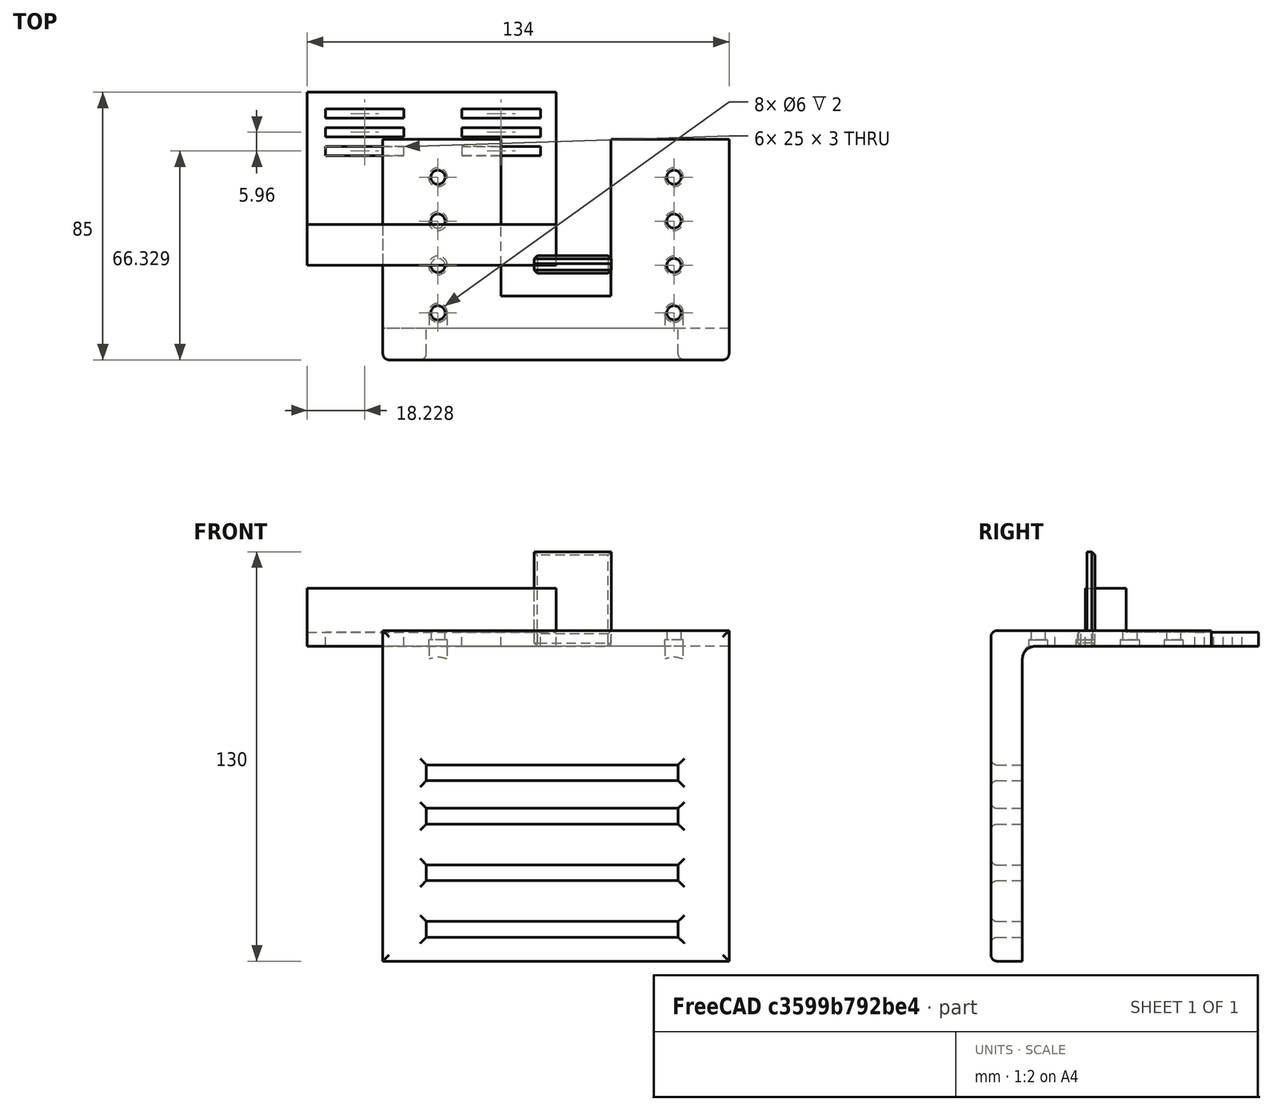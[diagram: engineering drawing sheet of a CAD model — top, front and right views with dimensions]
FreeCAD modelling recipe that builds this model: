
FCSTD DOCUMENT  (FreeCAD 1.2R20251230 (Git shallow))
Label: hook_1
License: Creative Commons Attribution 4.0
LicenseURL: https://creativecommons.org/licenses/by/4.0/
objects: TechDraw::DrawProjGroupItem×30, Sketcher::SketchObject×8, App::FeaturePython×8, PartDesign::Pad×5, App::Point×4, PartDesign::Pocket×3, PartDesign::Body×3, App::Link×3, TechDraw::DrawSVGTemplate×3, TechDraw::DrawProjGroup×3, TechDraw::DrawPage×3, PartDesign::Fillet×2, Assembly::JointGroup×1, PartDesign::Chamfer×1, Assembly::ViewGroup×1, Assembly::AssemblyObject×1
note: 52 computed .brp shape members not serialized (recipe doc carries the construction recipe); baked Part::Feature solids carry a one-line shape summary decoded from their .brp

FEATURE [App::Point] Origin001  label="原点"
  Role = Origin
FEATURE [Sketcher::SketchObject] Sketch
  ArcFitTolerance = 1e-06
  AttachmentSupport = -> [Origin]
  ExternalTypes = [0]
  FullyConstrained = false
  MakeInternals = false
  MapMode = 5
  sketch-geometry (16):
    g0: LineSegment StartX=-55 StartY=40 StartZ=0 EndX=-55 EndY=-30 EndZ=0
    g1: LineSegment StartX=-55 StartY=-30 StartZ=0 EndX=55 EndY=-30 EndZ=0
    g2: LineSegment StartX=55 StartY=-30 StartZ=0 EndX=55 EndY=40 EndZ=0
    g3: LineSegment StartX=55 StartY=40 StartZ=0 EndX=17.5 EndY=40 EndZ=0
    g4: Circle CenterX=-37.5 CenterY=0 CenterZ=0 NormalX=0 NormalY=0 NormalZ=1 AngleXU=0 Radius=2.25
    g5: Circle CenterX=37.5 CenterY=0 CenterZ=0 NormalX=0 NormalY=0 NormalZ=1 AngleXU=0 Radius=2.25
    g6: Circle CenterX=-37.5 CenterY=14.0912 CenterZ=0 NormalX=0 NormalY=0 NormalZ=1 AngleXU=0 Radius=2.25
    g7: Circle CenterX=37.5 CenterY=14.0912 CenterZ=0 NormalX=0 NormalY=0 NormalZ=1 AngleXU=0 Radius=2.25
    g8: Circle CenterX=-37.5 CenterY=-15.0582 CenterZ=0 NormalX=0 NormalY=0 NormalZ=1 AngleXU=0 Radius=2.25
    g9: Circle CenterX=37.5 CenterY=-15.0582 CenterZ=0 NormalX=0 NormalY=0 NormalZ=1 AngleXU=0 Radius=2.25
    g10: Circle CenterX=-37.5 CenterY=28.0083 CenterZ=0 NormalX=0 NormalY=0 NormalZ=1 AngleXU=0 Radius=2.25
    g11: Circle CenterX=37.5 CenterY=28.0083 CenterZ=0 NormalX=0 NormalY=0 NormalZ=1 AngleXU=0 Radius=2.25
    g12: LineSegment StartX=17.5 StartY=40 StartZ=0 EndX=17.5 EndY=-9.65989 EndZ=0
    g13: LineSegment StartX=17.5 StartY=-9.65989 StartZ=0 EndX=-17.5 EndY=-9.65989 EndZ=0
    g14: LineSegment StartX=-17.5 StartY=-9.65989 StartZ=0 EndX=-17.5 EndY=40 EndZ=0
    g15: LineSegment StartX=-17.5 StartY=40 StartZ=0 EndX=-55 EndY=40 EndZ=0
  constraints (27):
    c: Coincident(g0,g1)
    c: Coincident(g1,g2)
    c: Coincident(g2,g3)
    c: Coincident(g15,g0)
    c: Vertical(g2)
    c: Horizontal(g1)
    c: Symmetric(g2,g0,g-2)
    c: DistanceY(g0,g0) = 70
    c: DistanceX(g15,g3) = 110
    c: PointOnObject(g4,g-1)
    c: Symmetric(g4,g5,g-2)
    c: Distance(g1,g-1) = 30
    c: Diameter(g10) = 4.5
    c: Diameter(g11) = 4.5
    c: Diameter(g7) = 4.5
    c: Diameter(g6) = 4.5
    c: Diameter(g8) = 4.5
    c: Diameter(g9) = 4.5
    c: Diameter(g5) = 4.5
    c: Diameter(g4) = 4.5
    c: Coincident(g12,g13)
    c: Coincident(g13,g14)
    c: Symmetric(g12,g13,g-2)
    c: Vertical(g12)
    c: Vertical(g14)
    c: Coincident(g12,g3)
    c: Coincident(g14,g15)
FEATURE [PartDesign::Pad] Pad
  Direction = (0,0,1)
  Length = 5
  Length2 = 10
  Profile = -> Sketch
  ReferenceAxis = -> Sketch [N_Axis]
  Refine = true
  SideType = 0
  Suppressed = false
  Type = 0
  Type2 = 0
FEATURE [Sketcher::SketchObject] Sketch001
  ArcFitTolerance = 1e-06
  AttachmentSupport = -> [Origin]
  ExternalGeometry = -> [Pad]
  ExternalTypes = [0,0,0,0,0,0,0,0]
  FullyConstrained = true
  MakeInternals = false
  MapMode = 5
  sketch-geometry (8):
    g0: Circle CenterX=-37.5 CenterY=14.0912 CenterZ=0 NormalX=0 NormalY=0 NormalZ=1 AngleXU=0 Radius=3
    g1: Circle CenterX=-37.5 CenterY=0 CenterZ=0 NormalX=0 NormalY=0 NormalZ=1 AngleXU=0 Radius=3
    g2: Circle CenterX=-37.5 CenterY=-15.0582 CenterZ=0 NormalX=0 NormalY=0 NormalZ=1 AngleXU=0 Radius=3
    g3: Circle CenterX=37.5 CenterY=14.0912 CenterZ=0 NormalX=0 NormalY=0 NormalZ=1 AngleXU=0 Radius=3
    g4: Circle CenterX=37.5 CenterY=0 CenterZ=0 NormalX=0 NormalY=0 NormalZ=1 AngleXU=0 Radius=3
    g5: Circle CenterX=37.5 CenterY=-15.0582 CenterZ=0 NormalX=0 NormalY=0 NormalZ=1 AngleXU=0 Radius=3
    g6: Circle CenterX=-37.5 CenterY=28.0083 CenterZ=0 NormalX=0 NormalY=0 NormalZ=1 AngleXU=0 Radius=3
    g7: Circle CenterX=37.5 CenterY=28.0083 CenterZ=0 NormalX=0 NormalY=0 NormalZ=1 AngleXU=0 Radius=3
  constraints (16):
    c: Coincident(g0,g-3)
    c: Coincident(g1,g-4)
    c: Coincident(g2,g-5)
    c: Coincident(g3,g-6)
    c: Coincident(g4,g-7)
    c: Coincident(g5,g-8)
    c: Equal(g0,g1)
    c: Equal(g1,g2)
    c: Equal(g2,g3)
    c: Equal(g3,g4)
    c: Equal(g4,g5)
    c: Diameter(g1) = 6
    c: Coincident(g6,g-9)
    c: Coincident(g7,g-10)
    c: Equal(g7,g3)
    c: Equal(g6,g0)
FEATURE [PartDesign::Pocket] Pocket
  BaseFeature = -> Pad
  Direction = (0,0,-1)
  Length = 2
  Length2 = 5
  Profile = -> Sketch001
  ReferenceAxis = -> Sketch001 [N_Axis]
  Refine = true
  Reversed = true
  SideType = 0
  Suppressed = false
  Type = 0
  Type2 = 0
FEATURE [Sketcher::SketchObject] Sketch002
  ArcFitTolerance = 1e-06
  AttachmentSupport = -> [Pocket]
  ExternalTypes = [0]
  FullyConstrained = false
  MakeInternals = false
  MapMode = 5
  Placement = pos=(55,0,0) rot=(0.57735,0.57735,0.57735;2.0944rad)
  sketch-geometry (4):
    g0: LineSegment StartX=-30 StartY=-3.4e-15 StartZ=0 EndX=-30 EndY=-100 EndZ=0
    g1: LineSegment StartX=-30 StartY=-100 StartZ=0 EndX=-20 EndY=-100 EndZ=0
    g2: LineSegment StartX=-20 StartY=-100 StartZ=0 EndX=-20 EndY=0 EndZ=0
    g3: LineSegment StartX=-20 StartY=0 StartZ=0 EndX=-30 EndY=-3.4e-15 EndZ=0
  constraints (9):
    c: Coincident(g0,g1)
    c: Coincident(g1,g2)
    c: Coincident(g2,g3)
    c: Coincident(g3,g0)
    c: Vertical(g2)
    c: Horizontal(g1)
    c: DistanceX(g1,g1) = 10
    c: DistanceY(g0,g0) = 100
    c: Tangent(g3,g-1)
FEATURE [PartDesign::Pad] Pad001
  BaseFeature = -> Pocket
  Direction = (1,0,0)
  Length = 110
  Length2 = 10
  Profile = -> Sketch002
  ReferenceAxis = -> Sketch002 [N_Axis]
  Refine = true
  Reversed = true
  SideType = 0
  Suppressed = false
  Type = 0
  Type2 = 0
FEATURE [PartDesign::Fillet] Fillet
  Base = -> Pad001 [Edge10]
  BaseFeature = -> Pad001
  Radius = 4
  Refine = true
  SupportTransform = false
  Suppressed = false
  UseAllEdges = false
FEATURE [Sketcher::SketchObject] Sketch003
  ArcFitTolerance = 1e-06
  AttachmentSupport = -> [Fillet]
  ExternalTypes = [0]
  FullyConstrained = false
  MakeInternals = false
  MapMode = 5
  Placement = pos=(0,-30,0) rot=(1,0,0;1.5708rad)
  sketch-geometry (19):
    g0: LineSegment [constr] StartX=-5.28874 StartY=4.98412 StartZ=0 EndX=-5.28874 EndY=-78.0159 EndZ=0
    g1: LineSegment StartX=-41.1803 StartY=-51.4474 StartZ=0 EndX=-41.1803 EndY=-56.4474 EndZ=0
    g2: LineSegment StartX=-41.1803 StartY=-56.4474 StartZ=0 EndX=38.8197 EndY=-56.4474 EndZ=0
    g3: LineSegment StartX=38.8197 StartY=-56.4474 StartZ=0 EndX=38.8197 EndY=-51.4474 EndZ=0
    g4: LineSegment StartX=38.8197 StartY=-51.4474 StartZ=0 EndX=-41.1803 EndY=-51.4474 EndZ=0
    g5: LineSegment StartX=-41.1803 StartY=-37.651 StartZ=0 EndX=-41.1803 EndY=-42.651 EndZ=0
    g6: LineSegment StartX=-41.1803 StartY=-42.651 StartZ=0 EndX=38.8197 EndY=-42.651 EndZ=0
    g7: LineSegment StartX=38.8197 StartY=-42.651 StartZ=0 EndX=38.8197 EndY=-37.651 EndZ=0
    g8: LineSegment StartX=38.8197 StartY=-37.651 StartZ=0 EndX=-41.1803 EndY=-37.651 EndZ=0
    g9: LineSegment [constr] StartX=-5.28874 StartY=-12.9917 StartZ=0 EndX=-5.28874 EndY=-95.9917 EndZ=0
    g10: LineSegment StartX=-41.1803 StartY=-69.4232 StartZ=0 EndX=-41.1803 EndY=-74.4232 EndZ=0
    g11: LineSegment StartX=-41.1803 StartY=-74.4232 StartZ=0 EndX=38.8197 EndY=-74.4232 EndZ=0
    g12: LineSegment StartX=38.8197 StartY=-74.4232 StartZ=0 EndX=38.8197 EndY=-69.4232 EndZ=0
    g13: LineSegment StartX=38.8197 StartY=-69.4232 StartZ=0 EndX=-41.1803 EndY=-69.4232 EndZ=0
    g14: LineSegment [constr] StartX=-5.28874 StartY=-30.9676 StartZ=0 EndX=-5.28874 EndY=-113.968 EndZ=0
    g15: LineSegment StartX=-41.1803 StartY=-87.3991 StartZ=0 EndX=-41.1803 EndY=-92.3991 EndZ=0
    g16: LineSegment StartX=-41.1803 StartY=-92.3991 StartZ=0 EndX=38.8197 EndY=-92.3991 EndZ=0
    g17: LineSegment StartX=38.8197 StartY=-92.3991 StartZ=0 EndX=38.8197 EndY=-87.3991 EndZ=0
    g18: LineSegment StartX=38.8197 StartY=-87.3991 StartZ=0 EndX=-41.1803 EndY=-87.3991 EndZ=0
  constraints (43):
    c: Vertical(g0)
    c: Coincident(g1,g2)
    c: Coincident(g2,g3)
    c: Coincident(g3,g4)
    c: Coincident(g4,g1)
    c: Vertical(g1)
    c: Vertical(g3)
    c: Horizontal(g2)
    c: Horizontal(g4)
    c: DistanceY(g3,g3) = 5
    c: DistanceX(g4,g4) = 80
    c: Coincident(g5,g6)
    c: Coincident(g6,g7)
    c: Coincident(g7,g8)
    c: Coincident(g8,g5)
    c: Vertical(g5)
    c: Vertical(g7)
    c: Horizontal(g6)
    c: Horizontal(g8)
    c: Equal(g3,g7)
    c: Equal(g4,g8)
    c: Vertical(g9)
    c: Vertical(g14)
    c: Coincident(g10,g11)
    c: Coincident(g15,g16)
    c: Coincident(g11,g12)
    c: Coincident(g16,g17)
    c: Coincident(g12,g13)
    c: Coincident(g17,g18)
    c: Coincident(g13,g10)
    c: Coincident(g18,g15)
    c: Vertical(g10)
    c: Vertical(g15)
    c: Vertical(g12)
    c: Vertical(g17)
    c: Horizontal(g11)
    c: Horizontal(g16)
    c: Horizontal(g13)
    c: Horizontal(g18)
    c: DistanceY(g12,g12) = 5
    c: DistanceY(g17,g17) = 5
    c: DistanceX(g13,g13) = 80
    c: DistanceX(g18,g18) = 80
FEATURE [PartDesign::Pocket] Pocket001
  BaseFeature = -> Fillet
  Direction = (0,1,-2e-16)
  Length = 5
  Length2 = 5
  Profile = -> Sketch003
  ReferenceAxis = -> Sketch003 [N_Axis]
  Refine = true
  SideType = 0
  Suppressed = false
  Type = 1
  Type2 = 0
FEATURE [App::Point] Origin003  label="原点002"
  Role = Origin
FEATURE [Sketcher::SketchObject] Sketch004
  ArcFitTolerance = 1e-06
  AttachmentSupport = -> [Origin002]
  ExternalTypes = [0]
  FullyConstrained = false
  MakeInternals = false
  MapMode = 5
  sketch-geometry (28):
    g0: LineSegment StartX=-79 StartY=55 StartZ=0 EndX=-79 EndY=0 EndZ=0
    g1: LineSegment StartX=-79 StartY=0 StartZ=0 EndX=0 EndY=0 EndZ=0
    g2: LineSegment StartX=0 StartY=0 StartZ=0 EndX=0 EndY=55 EndZ=0
    g3: LineSegment StartX=0 StartY=55 StartZ=0 EndX=-79 EndY=55 EndZ=0
    g4: LineSegment StartX=-73.2718 StartY=37.8289 StartZ=0 EndX=-73.2718 EndY=34.8289 EndZ=0
    g5: LineSegment StartX=-73.2718 StartY=34.8289 StartZ=0 EndX=-48.2718 EndY=34.8289 EndZ=0
    g6: LineSegment StartX=-48.2718 StartY=34.8289 StartZ=0 EndX=-48.2718 EndY=37.8289 EndZ=0
    g7: LineSegment StartX=-48.2718 StartY=37.8289 StartZ=0 EndX=-73.2718 EndY=37.8289 EndZ=0
    g8: LineSegment StartX=-29.947 StartY=37.8289 StartZ=0 EndX=-29.947 EndY=34.8289 EndZ=0
    g9: LineSegment StartX=-29.947 StartY=34.8289 StartZ=0 EndX=-4.947 EndY=34.8289 EndZ=0
    g10: LineSegment StartX=-4.947 StartY=34.8289 StartZ=0 EndX=-4.947 EndY=37.8289 EndZ=0
    g11: LineSegment StartX=-4.947 StartY=37.8289 StartZ=0 EndX=-29.947 EndY=37.8289 EndZ=0
    g12: LineSegment StartX=-73.2718 StartY=43.789 StartZ=0 EndX=-73.2718 EndY=40.789 EndZ=0
    g13: LineSegment StartX=-73.2718 StartY=40.789 StartZ=0 EndX=-48.2718 EndY=40.789 EndZ=0
    g14: LineSegment StartX=-48.2718 StartY=40.789 StartZ=0 EndX=-48.2718 EndY=43.789 EndZ=0
    g15: LineSegment StartX=-48.2718 StartY=43.789 StartZ=0 EndX=-73.2718 EndY=43.789 EndZ=0
    g16: LineSegment StartX=-29.947 StartY=43.789 StartZ=0 EndX=-29.947 EndY=40.789 EndZ=0
    g17: LineSegment StartX=-29.947 StartY=40.789 StartZ=0 EndX=-4.947 EndY=40.789 EndZ=0
    g18: LineSegment StartX=-4.947 StartY=40.789 StartZ=0 EndX=-4.947 EndY=43.789 EndZ=0
    g19: LineSegment StartX=-4.947 StartY=43.789 StartZ=0 EndX=-29.947 EndY=43.789 EndZ=0
    g20: LineSegment StartX=-73.2718 StartY=49.7492 StartZ=0 EndX=-73.2718 EndY=46.7492 EndZ=0
    g21: LineSegment StartX=-73.2718 StartY=46.7492 StartZ=0 EndX=-48.2718 EndY=46.7492 EndZ=0
    g22: LineSegment StartX=-48.2718 StartY=46.7492 StartZ=0 EndX=-48.2718 EndY=49.7492 EndZ=0
    g23: LineSegment StartX=-48.2718 StartY=49.7492 StartZ=0 EndX=-73.2718 EndY=49.7492 EndZ=0
    g24: LineSegment StartX=-29.947 StartY=49.7492 StartZ=0 EndX=-29.947 EndY=46.7492 EndZ=0
    g25: LineSegment StartX=-29.947 StartY=46.7492 StartZ=0 EndX=-4.947 EndY=46.7492 EndZ=0
    g26: LineSegment StartX=-4.947 StartY=46.7492 StartZ=0 EndX=-4.947 EndY=49.7492 EndZ=0
    g27: LineSegment StartX=-4.947 StartY=49.7492 StartZ=0 EndX=-29.947 EndY=49.7492 EndZ=0
  constraints (71):
    c: Coincident(g0,g1)
    c: Coincident(g1,g2)
    c: Coincident(g2,g3)
    c: Coincident(g3,g0)
    c: Vertical(g0)
    c: Vertical(g2)
    c: Horizontal(g1)
    c: Horizontal(g3)
    c: Coincident(g1,g-1)
    c: DistanceX(g1,g1) = 79
    c: DistanceY(g2,g2) = 55
    c: Coincident(g4,g5)
    c: Coincident(g5,g6)
    c: Coincident(g6,g7)
    c: Coincident(g7,g4)
    c: Vertical(g4)
    c: Vertical(g6)
    c: Horizontal(g5)
    c: Horizontal(g7)
    c: DistanceY(g4,g4) = 3
    c: DistanceX(g7,g7) = 25
    c: Coincident(g8,g9)
    c: Coincident(g9,g10)
    c: Coincident(g10,g11)
    c: Coincident(g11,g8)
    c: Vertical(g8)
    c: Vertical(g10)
    c: Horizontal(g9)
    c: Horizontal(g11)
    c: DistanceY(g8,g8) = 3
    c: DistanceX(g11,g11) = 25
    c: Coincident(g12,g13)
    c: Coincident(g20,g21)
    c: Coincident(g13,g14)
    c: Coincident(g21,g22)
    c: Coincident(g14,g15)
    c: Coincident(g22,g23)
    c: Coincident(g15,g12)
    c: Coincident(g23,g20)
    c: Vertical(g12)
    c: Vertical(g20)
    c: Vertical(g14)
    c: Vertical(g22)
    c: Horizontal(g13)
    c: Horizontal(g21)
    c: Horizontal(g15)
    c: Horizontal(g23)
    c: DistanceY(g12,g12) = 3
    c: DistanceY(g20,g20) = 3
    c: DistanceX(g15,g15) = 25
    c: DistanceX(g23,g23) = 25
    c: Coincident(g16,g17)
    c: Coincident(g24,g25)
    c: Coincident(g17,g18)
    c: Coincident(g25,g26)
    c: Coincident(g18,g19)
    c: Coincident(g26,g27)
    c: Coincident(g19,g16)
    c: Coincident(g27,g24)
    c: Vertical(g16)
    c: Vertical(g24)
    c: Vertical(g18)
    c: Vertical(g26)
    c: Horizontal(g17)
    c: Horizontal(g25)
    c: Horizontal(g19)
    c: Horizontal(g27)
    c: DistanceY(g16,g16) = 3
    c: DistanceY(g24,g24) = 3
    c: DistanceX(g19,g19) = 25
    c: DistanceX(g27,g27) = 25
FEATURE [PartDesign::Pad] Pad002
  Direction = (0,0,1)
  Length = 18.5
  Length2 = 10
  Profile = -> Sketch004
  ReferenceAxis = -> Sketch004 [N_Axis]
  Refine = true
  SideType = 0
  Suppressed = false
  Type = 0
  Type2 = 0
FEATURE [Sketcher::SketchObject] Sketch005
  ArcFitTolerance = 1e-06
  AttachmentSupport = -> [Pad002]
  ExternalTypes = [0]
  FullyConstrained = false
  MakeInternals = false
  MapMode = 5
  Placement = pos=(-79,0,0) rot=(0.57735,-0.57735,-0.57735;2.0944rad)
  sketch-geometry (4):
    g0: LineSegment StartX=-65 StartY=18.5 StartZ=0 EndX=-65 EndY=4.5 EndZ=0
    g1: LineSegment StartX=-65 StartY=4.5 StartZ=0 EndX=-13 EndY=4.5 EndZ=0
    g2: LineSegment StartX=-13 StartY=4.5 StartZ=0 EndX=-13 EndY=18.5 EndZ=0
    g3: LineSegment StartX=-13 StartY=18.5 StartZ=0 EndX=-65 EndY=18.5 EndZ=0
  constraints (11):
    c: Coincident(g0,g1)
    c: Coincident(g1,g2)
    c: Coincident(g2,g3)
    c: Coincident(g3,g0)
    c: Vertical(g0)
    c: Vertical(g2)
    c: Horizontal(g1)
    c: Horizontal(g3)
    c: DistanceY(g2,g2) = 14
    c: DistanceX(g1,g1) = 52
    c: Distance(g-2,g2) = 13
FEATURE [PartDesign::Pocket] Pocket002
  BaseFeature = -> Pad002
  Direction = (1,0,0)
  Length = 5
  Length2 = 5
  Profile = -> Sketch005
  ReferenceAxis = -> Sketch005 [N_Axis]
  Refine = true
  SideType = 0
  Suppressed = false
  Type = 1
  Type2 = 0
FEATURE [PartDesign::Body] Body001  label="距离卡扣锁"
  AllowCompound = true
  Group = -> [Sketch004,Pad002,Sketch005,Pocket002]
  Origin = -> Origin002
  Tip = -> Pocket002
FEATURE [App::Point] Origin005  label="原点004"
  Role = Origin
FEATURE [App::Link] 锁  label="锁001"
  LinkPlacement = pos=(63.3611,109.371,72.3515) rot=(0,0.999048,-0.043619;3.14159rad)
  LinkedObject = -> Body001
  Placement = pos=(63.3611,109.371,72.3515) rot=(0,0.999048,-0.043619;3.14159rad)
FEATURE [App::Link] 主体背板  label="主体背板001"
  LinkPlacement = pos=(103.999,115.889,-20.7509) rot=(1,0,0;3.05433rad)
  LinkedObject = -> Body
  Placement = pos=(103.999,115.889,-20.7509) rot=(1,0,0;3.05433rad)
FEATURE [App::FeaturePython] Joint  label="平行"  # Assembly joint (typed FeaturePython)
  Angle = 0
  AngleMax = 0
  AngleMin = 0
  Detach1 = false
  Detach2 = false
  Distance = 0
  Distance2 = 0
  EnableAngleMax = false
  EnableAngleMin = false
  EnableLengthMax = false
  EnableLengthMin = false
  JointType = 6 (Parallel)
  LengthMax = 0
  LengthMin = 0
  Placement1 = pos=(-79,1.42e-14,0) rot=(-0.57735,-0.57735,0.57735;4.18879rad)
  Placement2 = pos=(55,5,5) rot=(0.57735,0.57735,0.57735;4.18879rad)
  Reference1 = -> Assembly [锁.Edge1,锁.Vertex2]
  Reference2 = -> Assembly [主体背板.?Edge26,主体背板.?Edge26]
  Suppressed = false
FEATURE [App::Point] Origin007  label="原点006"
  Role = Origin
FEATURE [Sketcher::SketchObject] Sketch006
  ArcFitTolerance = 1e-06
  AttachmentSupport = -> [Origin006]
  ExternalTypes = [0]
  FullyConstrained = false
  MakeInternals = false
  MapMode = 5
  sketch-geometry (4):
    g0: LineSegment StartX=-6.88135 StartY=0.564191 StartZ=0 EndX=17.6186 EndY=0.564191 EndZ=0
    g1: LineSegment StartX=17.6186 StartY=0.564191 StartZ=0 EndX=17.6186 EndY=3.06419 EndZ=0
    g2: LineSegment StartX=17.6186 StartY=3.06419 StartZ=0 EndX=-6.88135 EndY=3.06419 EndZ=0
    g3: LineSegment StartX=-6.88135 StartY=3.06419 StartZ=0 EndX=-6.88135 EndY=0.564191 EndZ=0
  constraints (10):
    c: Coincident(g0,g1)
    c: Coincident(g1,g2)
    c: Coincident(g2,g3)
    c: Coincident(g3,g0)
    c: Horizontal(g0)
    c: Horizontal(g2)
    c: Vertical(g1)
    c: Vertical(g3)
    c: DistanceY(g1,g1) = 2.5
    c: DistanceX(g2,g2) = 24.5
FEATURE [PartDesign::Pad] Pad003
  Direction = (0,0,1)
  Length = 30
  Length2 = 10
  Profile = -> Sketch006
  ReferenceAxis = -> Sketch006 [N_Axis]
  Refine = true
  SideType = 0
  Suppressed = false
  Type = 0
  Type2 = 0
FEATURE [App::FeaturePython] GroundedJoint  label="GroundedJoint001"  # Assembly grounded joint (typed FeaturePython)
  ObjectToGround = -> 主体背板
FEATURE [App::FeaturePython] GroundedJoint001  label="GroundedJoint002"  # Assembly grounded joint (typed FeaturePython)
  ObjectToGround = -> 锁
FEATURE [App::Link] 楔子  label="楔子001"
  LinkPlacement = pos=(85.7387,158.326,57.6818) rot=(0,0.043619,0.999048;3.14159rad)
  LinkedObject = -> Body002
  Placement = pos=(85.7387,158.326,57.6818) rot=(0,0.043619,0.999048;3.14159rad)
FEATURE [App::FeaturePython] Joint001  label="平行004"  # Assembly joint (typed FeaturePython)
  Angle = 0
  AngleMax = 0
  AngleMin = 0
  Detach1 = false
  Detach2 = false
  Distance = 0
  Distance2 = 0
  EnableAngleMax = false
  EnableAngleMin = false
  EnableLengthMax = false
  EnableLengthMin = false
  JointType = 6 (Parallel)
  LengthMax = 0
  LengthMin = 0
  Placement1 = pos=(-6.88135,3.06419,30) rot=(0,-0.707107,0.707107;3.14159rad)
  Placement2 = pos=(7.1e-15,55,0) rot=(0,-0.707107,0.707107;3.14159rad)
  Reference1 = -> Assembly [楔子.?Face5,楔子.?Vertex8]
  Reference2 = -> Assembly [锁.Face7,锁.Vertex8]
  Suppressed = false
FEATURE [Assembly::JointGroup] Joints
  Group = -> [Joint,GroundedJoint,GroundedJoint001,Joint001]
FEATURE [PartDesign::Fillet] Fillet001
  Base = -> Pocket001 [Face22]
  BaseFeature = -> Pocket001
  Radius = 2
  Refine = true
  SupportTransform = false
  Suppressed = false
  UseAllEdges = false
FEATURE [PartDesign::Body] Body  label="主体背板"
  AllowCompound = true
  Group = -> [Sketch,Pad,Sketch001,Pocket,Sketch002,Pad001,Fillet,Sketch003,Pocket001,Fillet001]
  Origin = -> Origin
  Tip = -> Fillet001
FEATURE [Sketcher::SketchObject] Sketch007
  ArcFitTolerance = 1e-06
  AttachmentSupport = -> [Pad003]
  ExternalTypes = [0,0]
  FullyConstrained = false
  MakeInternals = false
  MapMode = 5
  Placement = pos=(0,0.564191,0) rot=(1,0,0;1.5708rad)
  sketch-geometry (4):
    g0: LineSegment StartX=17.6186 StartY=0 StartZ=0 EndX=17.6186 EndY=5 EndZ=0
    g1: LineSegment StartX=17.6186 StartY=5 StartZ=0 EndX=-6.88135 EndY=5 EndZ=0
    g2: LineSegment StartX=-6.88135 StartY=5 StartZ=0 EndX=-6.88135 EndY=0 EndZ=0
    g3: LineSegment StartX=-6.88135 StartY=0 StartZ=0 EndX=17.6186 EndY=0 EndZ=0
  constraints (9):
    c: Coincident(g0,g1)
    c: Coincident(g1,g2)
    c: Coincident(g2,g3)
    c: Coincident(g3,g0)
    c: Vertical(g0)
    c: Vertical(g2)
    c: Horizontal(g1)
    c: Horizontal(g3)
    c: DistanceY(g0,g0) = 5
FEATURE [PartDesign::Pad] Pad004
  BaseFeature = -> Pad003
  Direction = (0,-1,2e-16)
  Length = 3
  Length2 = 10
  Profile = -> Sketch007
  ReferenceAxis = -> Sketch007 [N_Axis]
  Refine = true
  SideType = 0
  Suppressed = false
  Type = 0
  Type2 = 0
FEATURE [PartDesign::Chamfer] Chamfer
  Angle = 45
  Base = -> Pad004 [Face4,Face8,Face5]
  BaseFeature = -> Pad004
  ChamferType = 0
  FlipDirection = false
  Refine = true
  Size = 1
  Size2 = 1
  SupportTransform = false
  Suppressed = false
  UseAllEdges = false
FEATURE [PartDesign::Body] Body002  label="距离卡扣锁楔子"
  AllowCompound = true
  Group = -> [Sketch006,Pad003,Sketch007,Pad004,Chamfer]
  Origin = -> Origin006
  Tip = -> Chamfer
FEATURE [App::FeaturePython] Move  # WARN: FeaturePython — macro-defined, semantics opaque (R4)
  MoveType = 1
  References = -> Assembly [主体背板.,锁.,楔子.]
FEATURE [App::FeaturePython] Exploded_View  label="Exploded_View001"  # WARN: FeaturePython — macro-defined, semantics opaque (R4)
  Group = -> [Move]
FEATURE [App::FeaturePython] Move001  # WARN: FeaturePython — macro-defined, semantics opaque (R4)
  MoveType = 1
  MovementTransform = pos=(-3.17892e-06,-1.59465e-05,3.66656e-06) rot=(0,0,1;0rad)
  References = -> Assembly [锁.,主体背板.,楔子.]
FEATURE [App::FeaturePython] Exploded_View001  label="Exploded_View002"  # WARN: FeaturePython — macro-defined, semantics opaque (R4)
  Group = -> [Move001]
FEATURE [Assembly::ViewGroup] Exploded_Views
  Group = -> [Exploded_View,Exploded_View001]
FEATURE [Assembly::AssemblyObject] Assembly
  Group = -> [Joints,锁,主体背板,Joint,GroundedJoint,GroundedJoint001,楔子,Joint001,Exploded_Views,Exploded_View,Move,Exploded_View001,Move001]
  Origin = -> Origin004
  Type = Assembly
FEATURE [TechDraw::DrawSVGTemplate] Template  label="模板"
  Height = 420
  Orientation = 1
  Template = D:/Program Files (x86)/FreeCAD_weekly-2025.12.31-Windows-x86_64-py311/data/Mod/TechDraw/Templates/ISO/A2_Landscape_blank.svg
  Width = 594
FEATURE [TechDraw::DrawProjGroupItem] View  label="Front"
  CoarseView = false
  Direction = (0,-1,0)
  Focus = 100
  HardHidden = false
  IsoCount = 0
  IsoHidden = false
  IsoVisible = false
  LockPosition = true
  Perspective = false
  Rotation = 0
  RotationVector = (1,0,0)
  ScaleType = 2
  ScrubCount = 1
  SeamHidden = false
  SeamVisible = false
  SmoothHidden = false
  SmoothVisible = true
  Source = -> [Body]
  Type = 0
  X = 0
  XDirection = (1,0,0)
  Y = 0
FEATURE [TechDraw::DrawProjGroupItem] ProjItem  label="前右下"
  CoarseView = false
  Direction = (0.57735,-0.57735,-0.57735)
  Focus = 100
  HardHidden = false
  IsoCount = 0
  IsoHidden = false
  IsoVisible = false
  LockPosition = false
  Perspective = false
  Rotation = 0
  RotationVector = (1,0,0)
  ScaleType = 0
  ScrubCount = 1
  SeamHidden = false
  SeamVisible = false
  SmoothHidden = false
  SmoothVisible = true
  Source = -> [Body]
  Type = 9
  X = 133.229
  XDirection = (0.707107,0.707107,0)
  Y = -121.516
FEATURE [TechDraw::DrawProjGroupItem] ProjItem001  label="底视"
  CoarseView = false
  Direction = (0,0,-1)
  Focus = 100
  HardHidden = false
  IsoCount = 0
  IsoHidden = false
  IsoVisible = false
  LockPosition = false
  Perspective = false
  Rotation = 0
  RotationVector = (1,0,0)
  ScaleType = 0
  ScrubCount = 1
  SeamHidden = false
  SeamVisible = false
  SmoothHidden = false
  SmoothVisible = true
  Source = -> [Body]
  Type = 5
  X = 0
  XDirection = (1,0,0)
  Y = -121.516
FEATURE [TechDraw::DrawProjGroupItem] ProjItem002  label="前左下"
  CoarseView = false
  Direction = (-0.57735,-0.57735,-0.57735)
  Focus = 100
  HardHidden = false
  IsoCount = 0
  IsoHidden = false
  IsoVisible = false
  LockPosition = false
  Perspective = false
  Rotation = 0
  RotationVector = (1,0,0)
  ScaleType = 0
  ScrubCount = 1
  SeamHidden = false
  SeamVisible = false
  SmoothHidden = false
  SmoothVisible = true
  Source = -> [Body]
  Type = 8
  X = -133.229
  XDirection = (0.707107,-0.707107,0)
  Y = -121.516
FEATURE [TechDraw::DrawProjGroupItem] ProjItem003  label="右视"
  CoarseView = false
  Direction = (1,-1e-16,0)
  Focus = 100
  HardHidden = false
  IsoCount = 0
  IsoHidden = false
  IsoVisible = false
  LockPosition = false
  Perspective = false
  Rotation = 0
  RotationVector = (1,0,0)
  ScaleType = 0
  ScrubCount = 1
  SeamHidden = false
  SeamVisible = false
  SmoothHidden = false
  SmoothVisible = true
  Source = -> [Body]
  Type = 2
  X = 133.229
  XDirection = (1e-16,1,0)
  Y = 0
FEATURE [TechDraw::DrawProjGroupItem] ProjItem004  label="前右上"
  CoarseView = false
  Direction = (0.57735,-0.57735,0.57735)
  Focus = 100
  HardHidden = false
  IsoCount = 0
  IsoHidden = false
  IsoVisible = false
  LockPosition = false
  Perspective = false
  Rotation = 0
  RotationVector = (1,0,0)
  ScaleType = 0
  ScrubCount = 1
  SeamHidden = false
  SeamVisible = false
  SmoothHidden = false
  SmoothVisible = true
  Source = -> [Body]
  Type = 7
  X = 133.229
  XDirection = (0.707107,0.707107,0)
  Y = 133.764
FEATURE [TechDraw::DrawProjGroupItem] ProjItem005  label="俯视"
  CoarseView = false
  Direction = (0,0,1)
  Focus = 100
  HardHidden = false
  IsoCount = 0
  IsoHidden = false
  IsoVisible = false
  LockPosition = false
  Perspective = false
  Rotation = 0
  RotationVector = (1,0,0)
  ScaleType = 0
  ScrubCount = 1
  SeamHidden = false
  SeamVisible = false
  SmoothHidden = false
  SmoothVisible = true
  Source = -> [Body]
  Type = 4
  X = 0
  XDirection = (1,0,0)
  Y = 133.764
FEATURE [TechDraw::DrawProjGroupItem] ProjItem006  label="前左上"
  CoarseView = false
  Direction = (-0.57735,-0.57735,0.57735)
  Focus = 100
  HardHidden = false
  IsoCount = 0
  IsoHidden = false
  IsoVisible = false
  LockPosition = false
  Perspective = false
  Rotation = 0
  RotationVector = (1,0,0)
  ScaleType = 0
  ScrubCount = 1
  SeamHidden = false
  SeamVisible = false
  SmoothHidden = false
  SmoothVisible = true
  Source = -> [Body]
  Type = 6
  X = -133.229
  XDirection = (0.707107,-0.707107,0)
  Y = 133.764
FEATURE [TechDraw::DrawProjGroupItem] ProjItem007  label="左视"
  CoarseView = false
  Direction = (-1,-1e-16,0)
  Focus = 100
  HardHidden = false
  IsoCount = 0
  IsoHidden = false
  IsoVisible = false
  LockPosition = false
  Perspective = false
  Rotation = 0
  RotationVector = (1,0,0)
  ScaleType = 0
  ScrubCount = 1
  SeamHidden = false
  SeamVisible = false
  SmoothHidden = false
  SmoothVisible = true
  Source = -> [Body]
  Type = 1
  X = -133.229
  XDirection = (1e-16,-1,0)
  Y = 0
FEATURE [TechDraw::DrawProjGroupItem] ProjItem008  label="后视"
  CoarseView = false
  Direction = (0,1,0)
  Focus = 100
  HardHidden = false
  IsoCount = 0
  IsoHidden = false
  IsoVisible = false
  LockPosition = false
  Perspective = false
  Rotation = 0
  RotationVector = (1,0,0)
  ScaleType = 0
  ScrubCount = 1
  SeamHidden = false
  SeamVisible = false
  SmoothHidden = false
  SmoothVisible = true
  Source = -> [Body]
  Type = 3
  X = 266.458
  XDirection = (-1,0,0)
  Y = 0
FEATURE [TechDraw::DrawProjGroup] ProjGroup
  Anchor = -> View
  AutoDistribute = true
  LockPosition = false
  ProjectionType = 1
  Rotation = 0
  ScaleType = 0
  Source = -> [Body]
  Views = -> [View,ProjItem,ProjItem001,ProjItem002,ProjItem003,ProjItem004,ProjItem005,ProjItem006,ProjItem007,ProjItem008]
  X = 247
  Y = 200
  spacingX = 15
  spacingY = 2
FEATURE [TechDraw::DrawPage] Page  label="主体背板002"
  KeepUpdated = true
  NextBalloonIndex = 1
  ProjectionType = 0
  Template = -> Template
  Views = -> [ProjGroup]
FEATURE [TechDraw::DrawSVGTemplate] Template001  label="模板001"
  Height = 297
  Orientation = 1
  Template = D:/Program Files (x86)/FreeCAD_weekly-2025.12.31-Windows-x86_64-py311/data/Mod/TechDraw/Templates/ISO/A3_Landscape_blank.svg
  Width = 420
FEATURE [TechDraw::DrawProjGroupItem] View001  label="Front001"
  CoarseView = false
  Direction = (0,-1,0)
  Focus = 100
  HardHidden = false
  IsoCount = 0
  IsoHidden = false
  IsoVisible = false
  LockPosition = true
  Perspective = false
  Rotation = 0
  RotationVector = (1,0,0)
  ScaleType = 2
  ScrubCount = 1
  SeamHidden = false
  SeamVisible = false
  SmoothHidden = false
  SmoothVisible = true
  Source = -> [Body001]
  Type = 0
  X = 0
  XDirection = (1,0,0)
  Y = 0
FEATURE [TechDraw::DrawProjGroupItem] ProjItem009  label="前右下001"
  CoarseView = false
  Direction = (0.57735,-0.57735,-0.57735)
  Focus = 100
  HardHidden = false
  IsoCount = 0
  IsoHidden = false
  IsoVisible = false
  LockPosition = false
  Perspective = false
  Rotation = 0
  RotationVector = (1,0,0)
  ScaleType = 0
  ScrubCount = 1
  SeamHidden = false
  SeamVisible = false
  SmoothHidden = false
  SmoothVisible = true
  Source = -> [Body001]
  Type = 9
  X = -96.8762
  XDirection = (0.707107,0.707107,0)
  Y = 74.1552
FEATURE [TechDraw::DrawProjGroupItem] ProjItem010  label="底视001"
  CoarseView = false
  Direction = (0,0,-1)
  Focus = 100
  HardHidden = false
  IsoCount = 0
  IsoHidden = false
  IsoVisible = false
  LockPosition = false
  Perspective = false
  Rotation = 0
  RotationVector = (1,0,0)
  ScaleType = 0
  ScrubCount = 1
  SeamHidden = false
  SeamVisible = false
  SmoothHidden = false
  SmoothVisible = true
  Source = -> [Body001]
  Type = 5
  X = 0
  XDirection = (1,0,0)
  Y = 74.1552
FEATURE [TechDraw::DrawProjGroupItem] ProjItem011  label="前左下001"
  CoarseView = false
  Direction = (-0.57735,-0.57735,-0.57735)
  Focus = 100
  HardHidden = false
  IsoCount = 0
  IsoHidden = false
  IsoVisible = false
  LockPosition = false
  Perspective = false
  Rotation = 0
  RotationVector = (1,0,0)
  ScaleType = 0
  ScrubCount = 1
  SeamHidden = false
  SeamVisible = false
  SmoothHidden = false
  SmoothVisible = true
  Source = -> [Body001]
  Type = 8
  X = 96.8762
  XDirection = (0.707107,-0.707107,0)
  Y = 74.1552
FEATURE [TechDraw::DrawProjGroupItem] ProjItem012  label="左视001"
  CoarseView = false
  Direction = (-1,-1e-16,0)
  Focus = 100
  HardHidden = false
  IsoCount = 0
  IsoHidden = false
  IsoVisible = false
  LockPosition = false
  Perspective = false
  Rotation = 0
  RotationVector = (1,0,0)
  ScaleType = 0
  ScrubCount = 1
  SeamHidden = false
  SeamVisible = false
  SmoothHidden = false
  SmoothVisible = true
  Source = -> [Body001]
  Type = 1
  X = 96.8762
  XDirection = (1e-16,-1,0)
  Y = 0
FEATURE [TechDraw::DrawProjGroupItem] ProjItem013  label="前左上001"
  CoarseView = false
  Direction = (-0.57735,-0.57735,0.57735)
  Focus = 100
  HardHidden = false
  IsoCount = 0
  IsoHidden = false
  IsoVisible = false
  LockPosition = false
  Perspective = false
  Rotation = 0
  RotationVector = (1,0,0)
  ScaleType = 0
  ScrubCount = 1
  SeamHidden = false
  SeamVisible = false
  SmoothHidden = false
  SmoothVisible = true
  Source = -> [Body001]
  Type = 6
  X = 96.8762
  XDirection = (0.707107,-0.707107,0)
  Y = -68.4398
FEATURE [TechDraw::DrawProjGroupItem] ProjItem014  label="前右上001"
  CoarseView = false
  Direction = (0.57735,-0.57735,0.57735)
  Focus = 100
  HardHidden = false
  IsoCount = 0
  IsoHidden = false
  IsoVisible = false
  LockPosition = false
  Perspective = false
  Rotation = 0
  RotationVector = (1,0,0)
  ScaleType = 0
  ScrubCount = 1
  SeamHidden = false
  SeamVisible = false
  SmoothHidden = false
  SmoothVisible = true
  Source = -> [Body001]
  Type = 7
  X = -96.8762
  XDirection = (0.707107,0.707107,0)
  Y = -68.4398
FEATURE [TechDraw::DrawProjGroupItem] ProjItem015  label="右视001"
  CoarseView = false
  Direction = (1,-1e-16,0)
  Focus = 100
  HardHidden = false
  IsoCount = 0
  IsoHidden = false
  IsoVisible = false
  LockPosition = false
  Perspective = false
  Rotation = 0
  RotationVector = (1,0,0)
  ScaleType = 0
  ScrubCount = 1
  SeamHidden = false
  SeamVisible = false
  SmoothHidden = false
  SmoothVisible = true
  Source = -> [Body001]
  Type = 2
  X = -96.8762
  XDirection = (1e-16,1,0)
  Y = 0
FEATURE [TechDraw::DrawProjGroupItem] ProjItem016  label="俯视001"
  CoarseView = false
  Direction = (0,0,1)
  Focus = 100
  HardHidden = false
  IsoCount = 0
  IsoHidden = false
  IsoVisible = false
  LockPosition = false
  Perspective = false
  Rotation = 0
  RotationVector = (1,0,0)
  ScaleType = 0
  ScrubCount = 1
  SeamHidden = false
  SeamVisible = false
  SmoothHidden = false
  SmoothVisible = true
  Source = -> [Body001]
  Type = 4
  X = 0
  XDirection = (1,0,0)
  Y = -68.4398
FEATURE [TechDraw::DrawProjGroupItem] ProjItem017  label="后视001"
  CoarseView = false
  Direction = (0,1,0)
  Focus = 100
  HardHidden = false
  IsoCount = 0
  IsoHidden = false
  IsoVisible = false
  LockPosition = false
  Perspective = false
  Rotation = 0
  RotationVector = (1,0,0)
  ScaleType = 0
  ScrubCount = 1
  SeamHidden = false
  SeamVisible = false
  SmoothHidden = false
  SmoothVisible = true
  Source = -> [Body001]
  Type = 3
  X = 193.752
  XDirection = (-1,0,0)
  Y = 0
FEATURE [TechDraw::DrawProjGroup] ProjGroup001
  Anchor = -> View001
  AutoDistribute = true
  LockPosition = false
  ProjectionType = 0
  Rotation = 0
  ScaleType = 0
  Source = -> [Body001]
  Views = -> [View001,ProjItem009,ProjItem010,ProjItem011,ProjItem012,ProjItem013,ProjItem014,ProjItem015,ProjItem016,ProjItem017]
  X = 160
  Y = 150
  spacingX = 10
  spacingY = 30
FEATURE [TechDraw::DrawPage] Page001  label="距离卡扣锁001"
  KeepUpdated = true
  NextBalloonIndex = 1
  ProjectionType = 0
  Template = -> Template001
  Views = -> [ProjGroup001]
FEATURE [TechDraw::DrawSVGTemplate] Template002  label="模板002"
  Height = 210
  Orientation = 1
  Template = D:/Program Files (x86)/FreeCAD_weekly-2025.12.31-Windows-x86_64-py311/data/Mod/TechDraw/Templates/ISO/A4_Landscape_blank.svg
  Width = 297
FEATURE [TechDraw::DrawProjGroupItem] View002  label="Front002"
  CoarseView = false
  Direction = (0,-1,0)
  Focus = 100
  HardHidden = false
  IsoCount = 0
  IsoHidden = false
  IsoVisible = false
  LockPosition = true
  Perspective = false
  Rotation = 0
  RotationVector = (1,0,0)
  ScaleType = 2
  ScrubCount = 1
  SeamHidden = false
  SeamVisible = false
  SmoothHidden = false
  SmoothVisible = true
  Source = -> [Body002]
  Type = 0
  X = 0
  XDirection = (1,0,0)
  Y = 0
FEATURE [TechDraw::DrawProjGroupItem] ProjItem018  label="前右下002"
  CoarseView = false
  Direction = (0.57735,-0.57735,-0.57735)
  Focus = 100
  HardHidden = false
  IsoCount = 0
  IsoHidden = false
  IsoVisible = false
  LockPosition = false
  Perspective = false
  Rotation = 0
  RotationVector = (1,0,0)
  ScaleType = 0
  ScrubCount = 1
  SeamHidden = false
  SeamVisible = false
  SmoothHidden = false
  SmoothVisible = true
  Source = -> [Body002]
  Type = 9
  X = -37.1495
  XDirection = (0.707107,0.707107,0)
  Y = 47.3506
FEATURE [TechDraw::DrawProjGroupItem] ProjItem019  label="底视002"
  CoarseView = false
  Direction = (0,0,-1)
  Focus = 100
  HardHidden = false
  IsoCount = 0
  IsoHidden = false
  IsoVisible = false
  LockPosition = false
  Perspective = false
  Rotation = 0
  RotationVector = (1,0,0)
  ScaleType = 0
  ScrubCount = 1
  SeamHidden = false
  SeamVisible = false
  SmoothHidden = false
  SmoothVisible = true
  Source = -> [Body002]
  Type = 5
  X = 0
  XDirection = (1,0,0)
  Y = 47.3506
FEATURE [TechDraw::DrawProjGroupItem] ProjItem020  label="前左下002"
  CoarseView = false
  Direction = (-0.57735,-0.57735,-0.57735)
  Focus = 100
  HardHidden = false
  IsoCount = 0
  IsoHidden = false
  IsoVisible = false
  LockPosition = false
  Perspective = false
  Rotation = 0
  RotationVector = (1,0,0)
  ScaleType = 0
  ScrubCount = 1
  SeamHidden = false
  SeamVisible = false
  SmoothHidden = false
  SmoothVisible = true
  Source = -> [Body002]
  Type = 8
  X = 37.1495
  XDirection = (0.707107,-0.707107,0)
  Y = 47.3506
FEATURE [TechDraw::DrawProjGroupItem] ProjItem021  label="左视002"
  CoarseView = false
  Direction = (-1,-1e-16,0)
  Focus = 100
  HardHidden = false
  IsoCount = 0
  IsoHidden = false
  IsoVisible = false
  LockPosition = false
  Perspective = false
  Rotation = 0
  RotationVector = (1,0,0)
  ScaleType = 0
  ScrubCount = 1
  SeamHidden = false
  SeamVisible = false
  SmoothHidden = false
  SmoothVisible = true
  Source = -> [Body002]
  Type = 1
  X = 37.1495
  XDirection = (1e-16,-1,0)
  Y = 0
FEATURE [TechDraw::DrawProjGroupItem] ProjItem022  label="前左上002"
  CoarseView = false
  Direction = (-0.57735,-0.57735,0.57735)
  Focus = 100
  HardHidden = false
  IsoCount = 0
  IsoHidden = false
  IsoVisible = false
  LockPosition = false
  Perspective = false
  Rotation = 0
  RotationVector = (1,0,0)
  ScaleType = 0
  ScrubCount = 1
  SeamHidden = false
  SeamVisible = false
  SmoothHidden = false
  SmoothVisible = true
  Source = -> [Body002]
  Type = 6
  X = 37.1495
  XDirection = (0.707107,-0.707107,0)
  Y = -47.7588
FEATURE [TechDraw::DrawProjGroupItem] ProjItem023  label="俯视002"
  CoarseView = false
  Direction = (0,0,1)
  Focus = 100
  HardHidden = false
  IsoCount = 0
  IsoHidden = false
  IsoVisible = false
  LockPosition = false
  Perspective = false
  Rotation = 0
  RotationVector = (1,0,0)
  ScaleType = 0
  ScrubCount = 1
  SeamHidden = false
  SeamVisible = false
  SmoothHidden = false
  SmoothVisible = true
  Source = -> [Body002]
  Type = 4
  X = 0
  XDirection = (1,0,0)
  Y = -47.7588
FEATURE [TechDraw::DrawProjGroupItem] ProjItem024  label="前右上002"
  CoarseView = false
  Direction = (0.57735,-0.57735,0.57735)
  Focus = 100
  HardHidden = false
  IsoCount = 0
  IsoHidden = false
  IsoVisible = false
  LockPosition = false
  Perspective = false
  Rotation = 0
  RotationVector = (1,0,0)
  ScaleType = 0
  ScrubCount = 1
  SeamHidden = false
  SeamVisible = false
  SmoothHidden = false
  SmoothVisible = true
  Source = -> [Body002]
  Type = 7
  X = -37.1495
  XDirection = (0.707107,0.707107,0)
  Y = -47.7588
FEATURE [TechDraw::DrawProjGroupItem] ProjItem025  label="右视002"
  CoarseView = false
  Direction = (1,-1e-16,0)
  Focus = 100
  HardHidden = false
  IsoCount = 0
  IsoHidden = false
  IsoVisible = false
  LockPosition = false
  Perspective = false
  Rotation = 0
  RotationVector = (1,0,0)
  ScaleType = 0
  ScrubCount = 1
  SeamHidden = false
  SeamVisible = false
  SmoothHidden = false
  SmoothVisible = true
  Source = -> [Body002]
  Type = 2
  X = -37.1495
  XDirection = (1e-16,1,0)
  Y = 0
FEATURE [TechDraw::DrawProjGroupItem] ProjItem026  label="后视002"
  CoarseView = false
  Direction = (0,1,0)
  Focus = 100
  HardHidden = false
  IsoCount = 0
  IsoHidden = false
  IsoVisible = false
  LockPosition = false
  Perspective = false
  Rotation = 0
  RotationVector = (1,0,0)
  ScaleType = 0
  ScrubCount = 1
  SeamHidden = false
  SeamVisible = false
  SmoothHidden = false
  SmoothVisible = true
  Source = -> [Body002]
  Type = 3
  X = 74.299
  XDirection = (-1,0,0)
  Y = 0
FEATURE [TechDraw::DrawProjGroup] ProjGroup002
  Anchor = -> View002
  AutoDistribute = true
  LockPosition = false
  ProjectionType = 0
  Rotation = 0
  ScaleType = 0
  Source = -> [Body002]
  Views = -> [View002,ProjItem018,ProjItem019,ProjItem020,ProjItem021,ProjItem022,ProjItem023,ProjItem024,ProjItem025,ProjItem026]
  X = 148.5
  Y = 105
  spacingX = 15
  spacingY = 15
FEATURE [TechDraw::DrawPage] Page002  label="距离卡扣锁楔子001"
  KeepUpdated = true
  NextBalloonIndex = 1
  ProjectionType = 0
  Template = -> Template002
  Views = -> [ProjGroup002]
